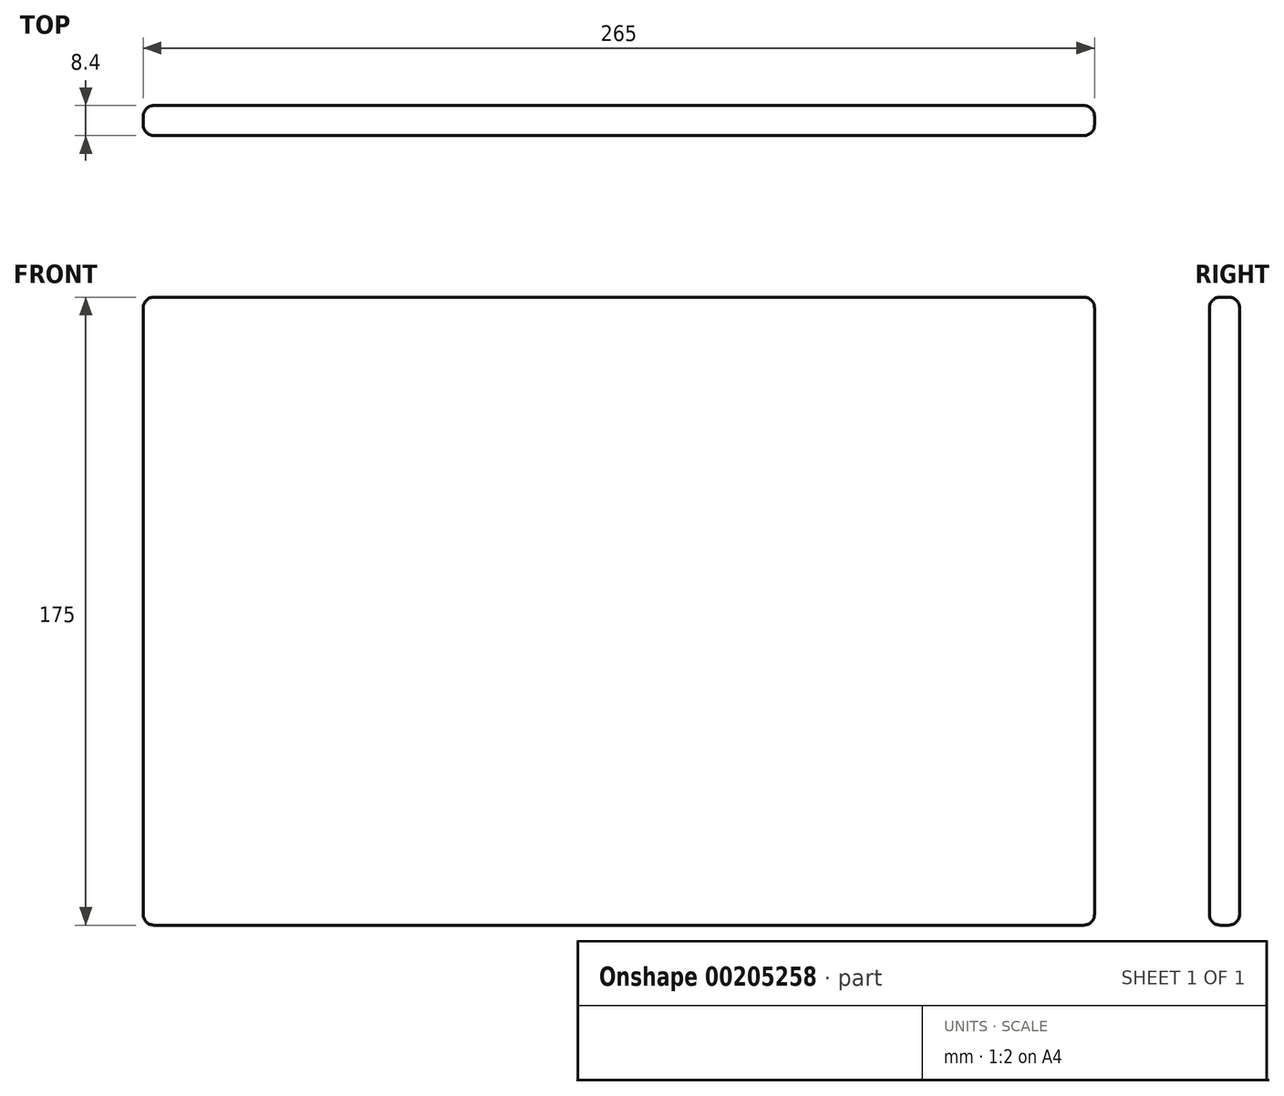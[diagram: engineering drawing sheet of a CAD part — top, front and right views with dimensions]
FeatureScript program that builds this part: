
annotation { "Feature Type Name" : "Feature", "Feature Type Description" : "" }
export const myFeature = defineFeature(function(context is Context, id is Id, definition is map)
    precondition{}
    {
        {
            var Q0;
            Q0=qCreatedBy(makeId("Front.planeOp"),FACE);
            var sketch = newSketch(context, id + "F0", { "sketchPlane" : qUnion([Q0])});
            skLineSegment(sketch, "E0.bottom", {"start": v(-39.01, 152.48) * mm, "end": v(225.99, 152.48) * mm});
            skLineSegment(sketch, "E0.top", {"start": v(-39.01, -22.52) * mm, "end": v(225.99, -22.52) * mm});
            skLineSegment(sketch, "E0.left", {"start": v(-39.01, 152.48) * mm, "end": v(-39.01, -22.52) * mm});
            skLineSegment(sketch, "E0.right", {"start": v(225.99, 152.48) * mm, "end": v(225.99, -22.52) * mm});
            skSolve(sketch);
        }
        {
            var Q0;
            Q0=makeQuery(id+"F0.imprint","IMPRINT",FACE,{"disambiguationData":[TD([[makeQuery(id+"F0.imprint","IMPRINT",EDGE,{"derivedFrom":sQuery(id+"F0.wireOp",EDGE,"E0.bottom")}),-1.0]])]});
            extrude(context, id + "F1", {"entities" : qUnion([Q0]), "depth" : 8.4 * mm});
        }
        {
            var Q0;
            Q0=makeQuery(id+"F1.opExtrude","CAP_EDGE",EDGE,{"disambiguationData":[OSD([sQuery(id+"F0.wireOp",EDGE,"E0.top")])],"isStart":false});
            var Q1;
            Q1=makeQuery(id+"F1.opExtrude","CAP_EDGE",EDGE,{"disambiguationData":[OSD([sQuery(id+"F0.wireOp",EDGE,"E0.top")])],"isStart":true});
            var Q2;
            Q2=makeQuery(id+"F1.opExtrude","CAP_EDGE",EDGE,{"disambiguationData":[OSD([sQuery(id+"F0.wireOp",EDGE,"E0.right")])],"isStart":true});
            var Q3;
            Q3=makeQuery(id+"F1.opExtrude","CAP_EDGE",EDGE,{"disambiguationData":[OSD([sQuery(id+"F0.wireOp",EDGE,"E0.right")])],"isStart":false});
            var Q4;
            Q4=makeQuery(id+"F1.opExtrude","SWEPT_EDGE",EDGE,{"disambiguationData":[OSD([sQuery(id+"F0.wireOp",EDGE,"E0.top"),sQuery(id+"F0.wireOp",EDGE,"E0.right")])]});
            var Q5;
            Q5=makeQuery(id+"F1.opExtrude","CAP_EDGE",EDGE,{"disambiguationData":[OSD([sQuery(id+"F0.wireOp",EDGE,"E0.left")])],"isStart":false});
            var Q6;
            Q6=makeQuery(id+"F1.opExtrude","CAP_EDGE",EDGE,{"disambiguationData":[OSD([sQuery(id+"F0.wireOp",EDGE,"E0.left")])],"isStart":true});
            var Q7;
            Q7=makeQuery(id+"F1.opExtrude","SWEPT_EDGE",EDGE,{"disambiguationData":[OSD([sQuery(id+"F0.wireOp",EDGE,"E0.top"),sQuery(id+"F0.wireOp",EDGE,"E0.left")])]});
            var Q8;
            Q8=makeQuery(id+"F1.opExtrude","SWEPT_EDGE",EDGE,{"disambiguationData":[OSD([sQuery(id+"F0.wireOp",EDGE,"E0.bottom"),sQuery(id+"F0.wireOp",EDGE,"E0.left")])]});
            var Q9;
            Q9=makeQuery(id+"F1.opExtrude","CAP_EDGE",EDGE,{"disambiguationData":[OSD([sQuery(id+"F0.wireOp",EDGE,"E0.bottom")])],"isStart":true});
            var Q10;
            Q10=makeQuery(id+"F1.opExtrude","CAP_EDGE",EDGE,{"disambiguationData":[OSD([sQuery(id+"F0.wireOp",EDGE,"E0.bottom")])],"isStart":false});
            var Q11;
            Q11=makeQuery(id+"F1.opExtrude","SWEPT_EDGE",EDGE,{"disambiguationData":[OSD([sQuery(id+"F0.wireOp",EDGE,"E0.bottom"),sQuery(id+"F0.wireOp",EDGE,"E0.right")])]});
            fillet(context, id + "F2", {"entities" : qUnion([Q0, Q1, Q2, Q3, Q4, Q5, Q6, Q7, Q8, Q9, Q10, Q11]), "radius" : 3 * mm, "tangentPropagation" : true, "allowEdgeOverflow" : false});
        }
    });
